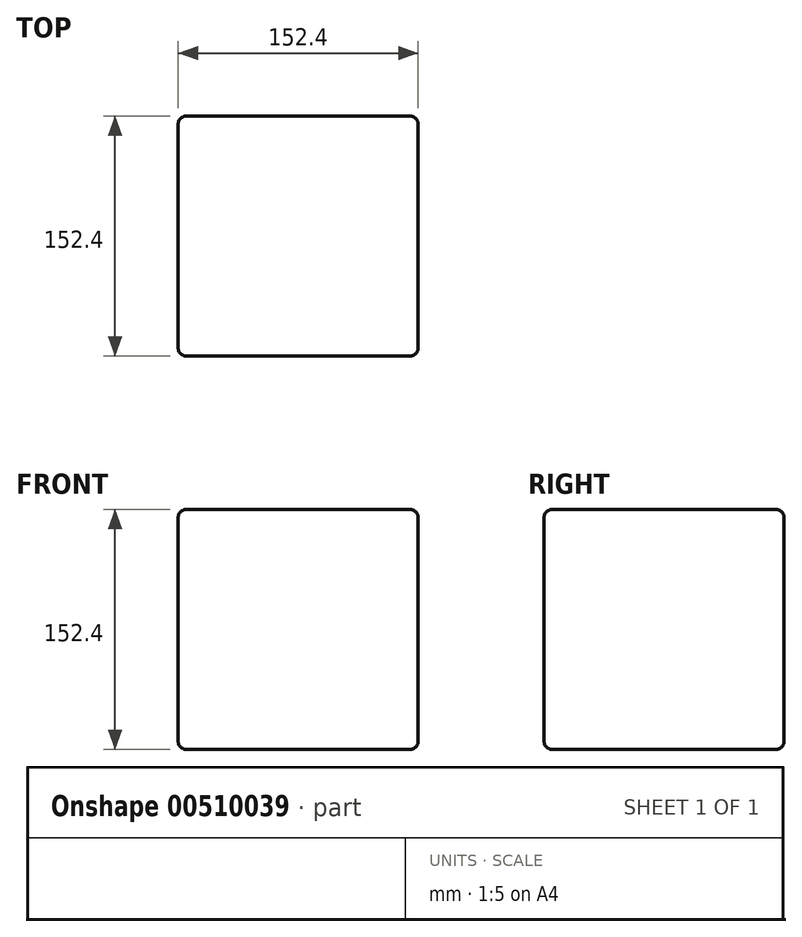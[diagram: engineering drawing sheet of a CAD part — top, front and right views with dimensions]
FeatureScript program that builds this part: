
annotation { "Feature Type Name" : "Feature", "Feature Type Description" : "" }
export const myFeature = defineFeature(function(context is Context, id is Id, definition is map)
    precondition{}
    {
        {
            var Q0;
            Q0=qCreatedBy(makeId("Top.planeOp"),FACE);
            var sketch = newSketch(context, id + "F0", { "sketchPlane" : qUnion([Q0])});
            skLineSegment(sketch, "E0.bottom", {"start": v(38.57, -34.12) * mm, "end": v(-113.83, -34.12) * mm});
            skLineSegment(sketch, "E0.top", {"start": v(38.57, 118.28) * mm, "end": v(-113.83, 118.28) * mm});
            skLineSegment(sketch, "E0.left", {"start": v(38.57, -34.12) * mm, "end": v(38.57, 118.28) * mm});
            skLineSegment(sketch, "E0.right", {"start": v(-113.83, -34.12) * mm, "end": v(-113.83, 118.28) * mm});
            skPoint(sketch, "E0.middle", {"position": v(-37.63, 42.08) * mm});
            skSolve(sketch);
        }
        {
            var Q0;
            Q0=makeQuery(id+"F0.imprint","IMPRINT",FACE,{"disambiguationData":[TD([[makeQuery(id+"F0.imprint","IMPRINT",EDGE,{"derivedFrom":sQuery(id+"F0.wireOp",EDGE,"E0.bottom")}),-1.0]])]});
            extrude(context, id + "F1", {"entities" : qUnion([Q0]), "oppositeDirection" : true, "depth" : 152.4 * mm});
        }
        {
            var Q0;
            Q0=makeQuery(id+"F1.opExtrude","SWEPT_EDGE",EDGE,{"disambiguationData":[OSD([sQuery(id+"F0.wireOp",EDGE,"E0.bottom"),sQuery(id+"F0.wireOp",EDGE,"E0.left")])]});
            fillet(context, id + "F2", {"entities" : qUnion([Q0]), "radius" : 5.08 * mm, "tangentPropagation" : true, "allowEdgeOverflow" : false});
        }
        {
            var Q0;
            Q0=makeQuery(id+"F1.opExtrude","CAP_EDGE",EDGE,{"disambiguationData":[OSD([sQuery(id+"F0.wireOp",EDGE,"E0.left")])],"isStart":true});
            fillet(context, id + "F3", {"entities" : qUnion([Q0]), "radius" : 5.08 * mm, "tangentPropagation" : true, "allowEdgeOverflow" : false});
        }
        {
            var Q0;
            Q0=makeQuery(id+"F1.opExtrude","SWEPT_FACE",FACE,{"disambiguationData":[OSD([sQuery(id+"F0.wireOp",EDGE,"E0.right")])]});
            fillet(context, id + "F4", {"entities" : qUnion([Q0]), "radius" : 5.08 * mm, "tangentPropagation" : true, "allowEdgeOverflow" : false});
        }
        {
            var Q0;
            Q0=makeQuery(id+"F1.opExtrude","SWEPT_FACE",FACE,{"disambiguationData":[OSD([sQuery(id+"F0.wireOp",EDGE,"E0.bottom")])]});
            fillet(context, id + "F5", {"entities" : qUnion([Q0]), "radius" : 5.08 * mm, "tangentPropagation" : true, "allowEdgeOverflow" : false});
        }
        {
            var Q0;
            Q0=makeQuery(id+"F1.opExtrude","SWEPT_FACE",FACE,{"disambiguationData":[OSD([sQuery(id+"F0.wireOp",EDGE,"E0.top")])]});
            fillet(context, id + "F6", {"entities" : qUnion([Q0]), "radius" : 5.08 * mm, "tangentPropagation" : true, "allowEdgeOverflow" : false});
        }
    });
